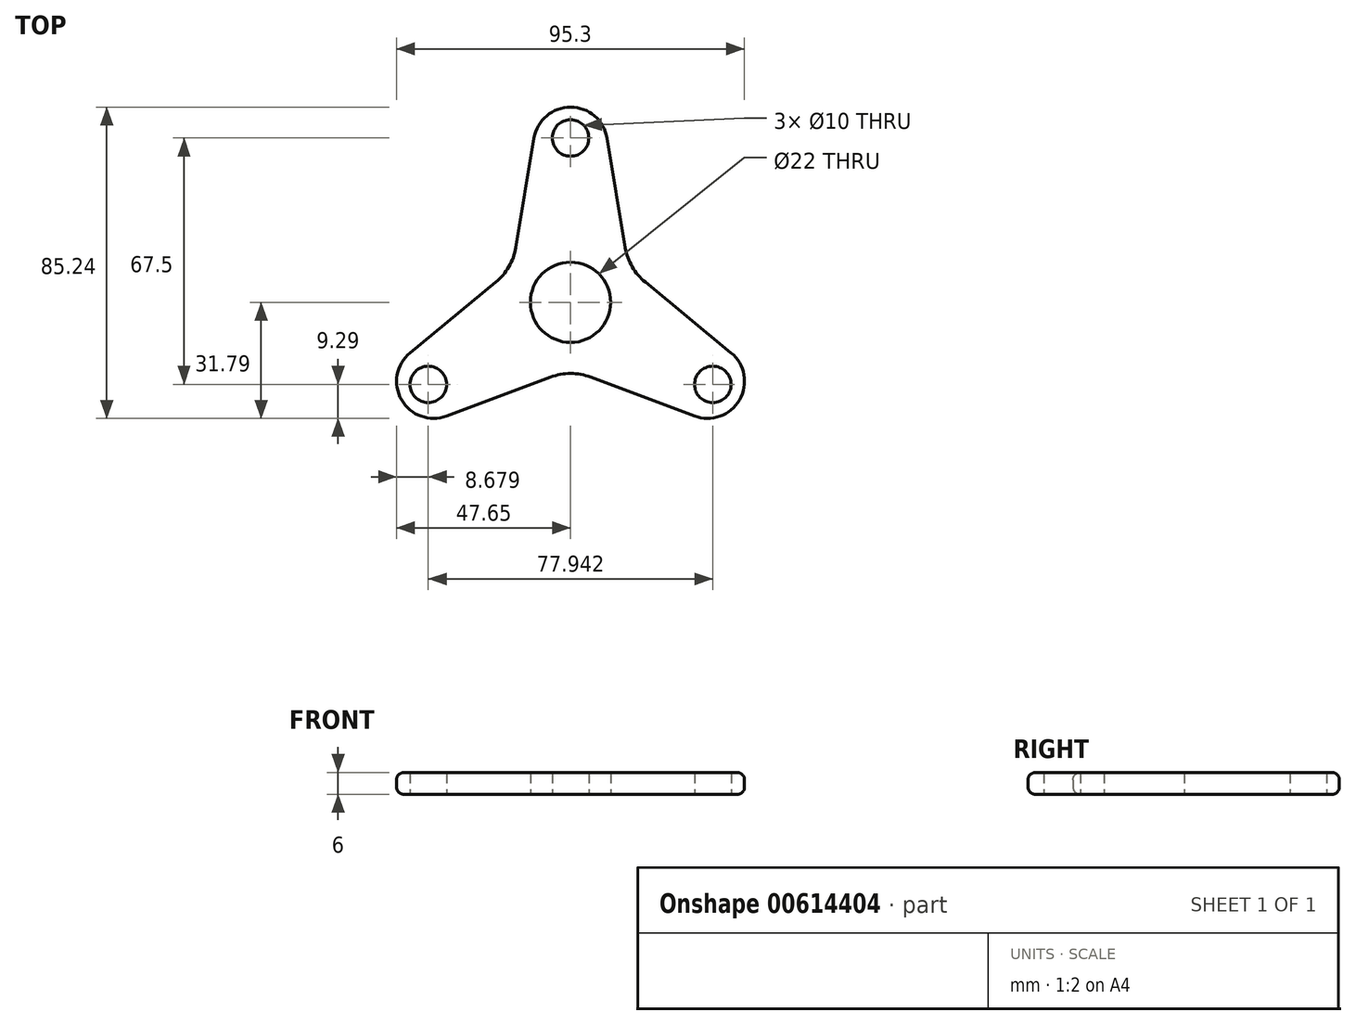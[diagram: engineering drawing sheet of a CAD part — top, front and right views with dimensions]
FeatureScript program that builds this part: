
annotation { "Feature Type Name" : "Feature", "Feature Type Description" : "" }
export const myFeature = defineFeature(function(context is Context, id is Id, definition is map)
    precondition{}
    {
        {
            var Q0;
            Q0=qCreatedBy(makeId("Top.planeOp"),FACE);
            var sketch = newSketch(context, id + "F0", { "sketchPlane" : qUnion([Q0])});
            skCircle(sketch, "E0", {"center": v(0, 0) * mm, "radius": 11 * mm});
            skCircle(sketch, "E1", {"center": v(0, 45) * mm, "radius": 5 * mm});
            skCircle(sketch, "E2.1.0", {"center": v(-38.97, -22.5) * mm, "radius": 5 * mm});
            skCircle(sketch, "E2.2.0", {"center": v(38.97, -22.5) * mm, "radius": 5 * mm});
            skLineSegment(sketch, "E3", {"start": v(-10, 44.98) * mm, "end": v(-15, 15) * mm});
            skLineSegment(sketch, "E4.1.0", {"start": v(-33.95, -31.15) * mm, "end": v(-5.5, -20.5) * mm});
            skLineSegment(sketch, "E4.2.0", {"start": v(43.95, -13.83) * mm, "end": v(20.5, 5.5) * mm});
            skLineSegment(sketch, "E5.MirrorCS", {"start": v(10, 44.98) * mm, "end": v(15, 15) * mm});
            skLineSegment(sketch, "E6.1.0", {"start": v(-43.95, -13.83) * mm, "end": v(-20.5, 5.5) * mm});
            skLineSegment(sketch, "E6.2.0", {"start": v(33.95, -31.15) * mm, "end": v(5.5, -20.5) * mm});
            skArc(sketch, "E7", {"start": v(-20.5, 5.5) * mm, "mid": v(-16.88, 9.75) * mm, "end": v(-15, 15) * mm});
            skArc(sketch, "E8", {"start": v(-43.95, -13.83) * mm, "mid": v(-46.29, -26.72) * mm, "end": v(-33.95, -31.15) * mm});
            skArc(sketch, "E9.1.1", {"start": v(5.5, -20.5) * mm, "mid": v(0, -19.5) * mm, "end": v(-5.5, -20.5) * mm});
            skArc(sketch, "E9.1.2", {"start": v(33.95, -31.15) * mm, "mid": v(46.29, -26.72) * mm, "end": v(43.95, -13.83) * mm});
            skArc(sketch, "E9.2.1", {"start": v(15, 15) * mm, "mid": v(16.88, 9.75) * mm, "end": v(20.5, 5.5) * mm});
            skArc(sketch, "E9.2.2", {"start": v(10, 44.98) * mm, "mid": v(0, 53.45) * mm, "end": v(-10, 44.98) * mm});
            skSolve(sketch);
        }
        {
            var Q0;
            Q0=makeQuery(id+"F0.imprint","IMPRINT",FACE,{"disambiguationData":[TD([[makeQuery(id+"F0.imprint","IMPRINT",EDGE,{"derivedFrom":sQuery(id+"F0.wireOp",EDGE,"E0")}),-1.0]])]});
            extrude(context, id + "F1", {"entities" : qUnion([Q0]), "depth" : 6 * mm, "offsetDistance" : 25 * mm});
        }
        {
            var Q0;
            Q0=makeQuery(id+"F1.opExtrude","CAP_EDGE",EDGE,{"disambiguationData":[OSD([sQuery(id+"F0.wireOp",EDGE,"E3")])],"isStart":false});
            var Q1;
            Q1=makeQuery(id+"F1.opExtrude","CAP_EDGE",EDGE,{"disambiguationData":[OSD([sQuery(id+"F0.wireOp",EDGE,"E3")])],"isStart":true});
            fillet(context, id + "F2", {"entities" : qUnion([Q0, Q1]), "radius" : 2 * mm, "tangentPropagation" : true, "allowEdgeOverflow" : false});
        }
    });
